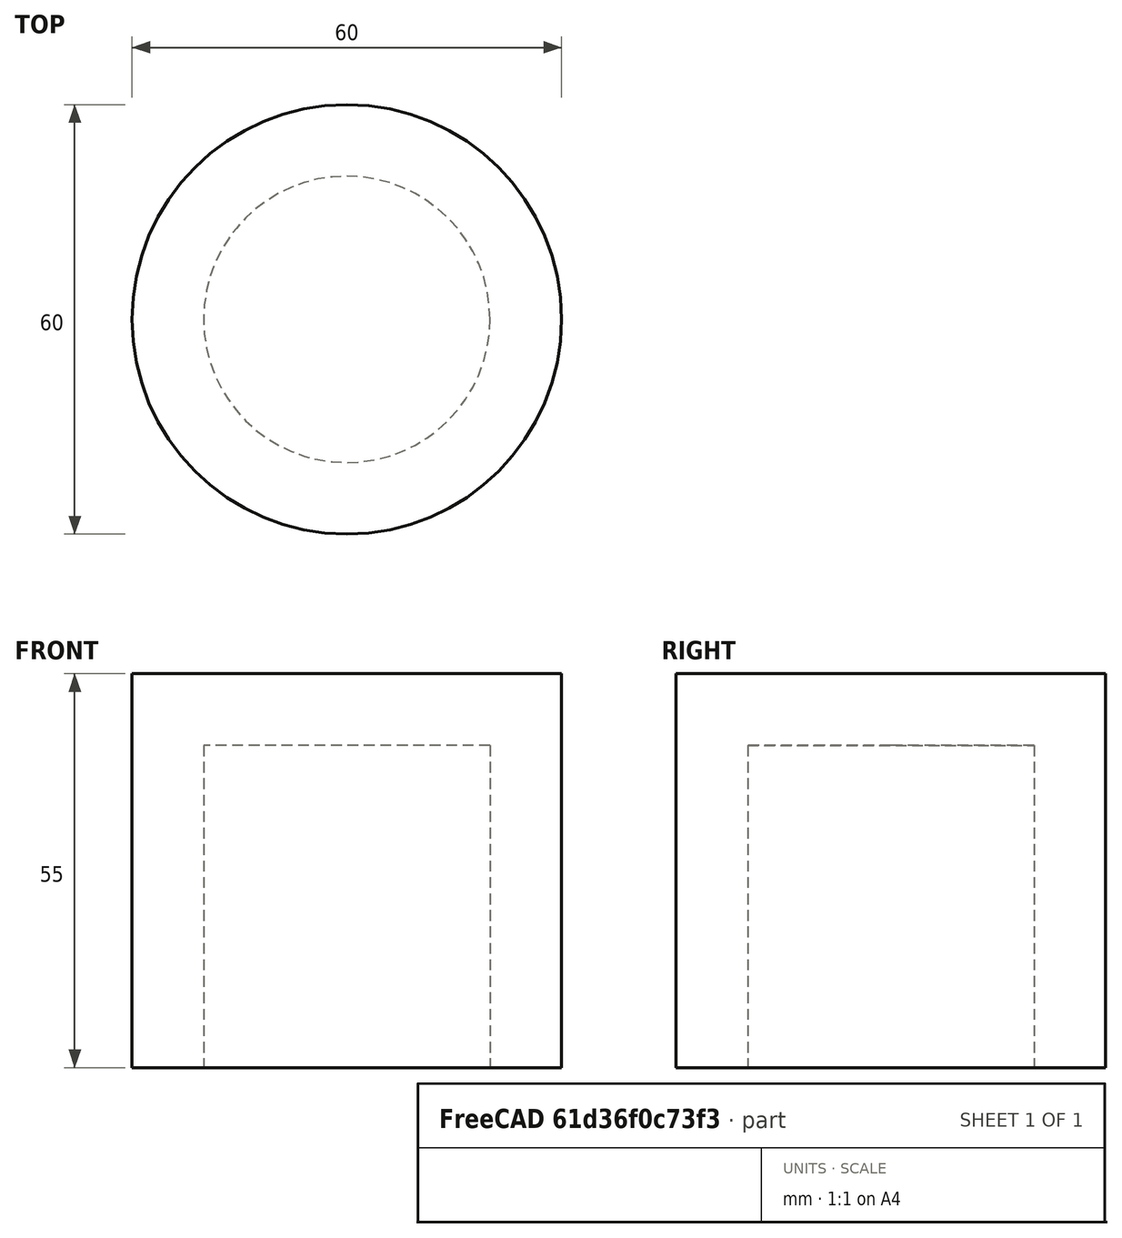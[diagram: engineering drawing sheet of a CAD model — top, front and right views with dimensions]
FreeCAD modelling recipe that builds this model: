
FCSTD DOCUMENT  (FreeCAD 0.20R29603 (Git))
Label: Piston In FreeCAD
License: All rights reserved
LicenseURL: http://en.wikipedia.org/wiki/All_rights_reserved
objects: Sketcher::SketchObject×2, PartDesign::Revolution×1, PartDesign::Body×1
note: 5 computed .brp shape members not serialized (recipe doc carries the construction recipe); baked Part::Feature solids carry a one-line shape summary decoded from their .brp

FEATURE [Sketcher::SketchObject] Sketch
  FullyConstrained = true
  MapMode = 5
  Placement = pos=(0,0,0) rot=(1,0,0;1.5708rad)
  Support = -> [XZ_Plane]
  sketch-geometry (6):
    g0: LineSegment StartX=0 StartY=55 StartZ=0 EndX=0 EndY=45 EndZ=0
    g1: LineSegment StartX=0 StartY=45 StartZ=0 EndX=20 EndY=45 EndZ=0
    g2: LineSegment StartX=20 StartY=45 StartZ=0 EndX=20 EndY=0 EndZ=0
    g3: LineSegment StartX=20 StartY=0 StartZ=0 EndX=30 EndY=0 EndZ=0
    g4: LineSegment StartX=30 StartY=0 StartZ=0 EndX=30 EndY=55 EndZ=0
    g5: LineSegment StartX=30 StartY=55 StartZ=0 EndX=0 EndY=55 EndZ=0
  constraints (18):
    c: Vertical(g0)
    c: Coincident(g0,g1)
    c: Horizontal(g1)
    c: Coincident(g1,g2)
    c: Vertical(g2)
    c: Coincident(g2,g3)
    c: Coincident(g3,g4)
    c: Coincident(g4,g5)
    c: Coincident(g5,g0)
    c: Horizontal(g5)
    c: Vertical(g4)
    c: Horizontal(g3)
    c: PointOnObject(g0,g-2)
    c: PointOnObject(g2,g-1)
    c: DistanceX(g3,g3) = 10
    c: Distance(g0) = 10
    c: Distance(g3,g-1) = 30
    c: Distance(g0,g-1) = 55
FEATURE [PartDesign::Revolution] Revolution
  Angle = 360
  Axis = (0,2e-16,1)
  Base = (0,0,0)
  Placement = pos=(0,0,0) rot=(1,0,0;1.5708rad)
  Profile = -> Sketch
  ReferenceAxis = -> Sketch [V_Axis]
  Reversed = true
FEATURE [Sketcher::SketchObject] Sketch001
  FullyConstrained = true
  MapMode = 5
  Placement = pos=(0,0,0) rot=(0.57735,0.57735,0.57735;2.0944rad)
  Support = -> [YZ_Plane]
  sketch-geometry (1):
    g0: Circle CenterX=0 CenterY=20 CenterZ=0 NormalX=0 NormalY=0 NormalZ=1 AngleXU=0 Radius=12.5
  constraints (3):
    c: PointOnObject(g0,g-2)
    c: Distance(g0,g-1) = 20
    c: Diameter(g0) = 25
FEATURE [PartDesign::Body] Body
  Group = -> [Sketch,Revolution,Sketch001]
  Origin = -> Origin
  Tip = -> Revolution
